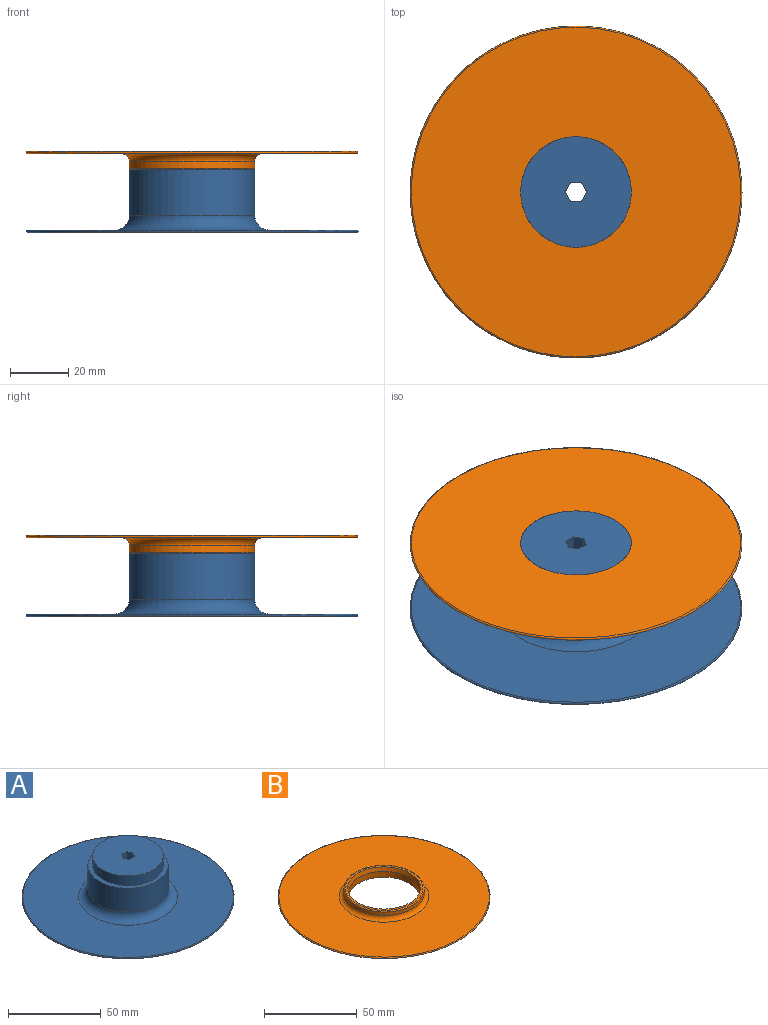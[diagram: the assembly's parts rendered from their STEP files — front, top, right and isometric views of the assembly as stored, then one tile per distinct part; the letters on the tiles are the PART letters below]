
ASSEMBLY  parts=2 mates=1
PART A: 14 faces, bbox 123.7x123.7x27.9 mm
  f0: plane 113.45x113.45mm, normal (0,0,1), area 7874.8mm2, adj f2,f13
  f1: plane 113.45x113.45mm, normal (0,0,-1), area 10074.5mm2, adj f2,f3,f4,f5,f6,f7,f9
  f2: torus R=56.73mm, axis (0,0,1), area 476.3mm2, adj f0,f1
  f3: plane 27.94x3.18mm, normal (0.87,-0.5,0), area 102.4mm2, adj f1,f4,f9,f10
  f4: plane 27.94x3.67mm, normal (0,-1,0), area 102.4mm2, adj f1,f3,f5,f10
  f5: plane 27.94x3.18mm, normal (-0.87,-0.5,0), area 102.4mm2, adj f1,f4,f6,f10
  f6: plane 27.94x3.18mm, normal (-0.87,0.5,0), area 102.4mm2, adj f1,f5,f7,f10
  f7: plane 27.94x3.67mm, normal (0,1,0), area 102.4mm2, adj f1,f6,f9,f10
  f8: cylinder r=19.05mm len=38.1mm, axis (0,0,-1), area 760.1mm2, adj f10,f12
  f9: plane 27.94x3.18mm, normal (0.87,0.5,0), area 102.4mm2, adj f1,f3,f7,f10
  f10: plane 38.1x38.1mm, normal (0,0,1), area 1105.2mm2, adj f3,f4,f5,f6,f7,f8,f9
  f11: cylinder r=21.59mm len=43.18mm, axis (0,0,-1), area 2124.8mm2, adj f12,f13
  f12: plane 43.18x43.18mm, normal (0,0,1), area 324.3mm2, adj f8,f11
  f13: torus R=26.67mm, axis (0,0,1), area 1175mm2, adj f0,f11
PART B: 9 faces, bbox 123.7x123.7x6.4 mm
  f0: plane 113.45x113.45mm, normal (0,0,1), area 8280.2mm2, adj f5,f7
  f1: plane 113.45x113.45mm, normal (0,0,-1), area 8969.3mm2, adj f2,f5
  f2: cylinder r=19.05mm len=38.1mm, axis (0,0,-1), area 456mm2, adj f1,f8
  f3: cylinder r=21.59mm len=43.18mm, axis (0,0,-1), area 315.8mm2, adj f6,f7
  f4: plane 41.91x41.91mm, normal (0,0,1), area 162.1mm2, adj f6,f8
  f5: torus R=56.73mm, axis (0,0,1), area 476.3mm2, adj f0,f1
  f6: torus R=20.96mm, axis (0,0,1), area 133.9mm2, adj f3,f4
  f7: torus R=24.13mm, axis (0,0,1), area 564.4mm2, adj f0,f3
  f8: cone r=19.05mm half-angle=14deg, axis (0,0,1), area 318.6mm2, adj f2,f4
PLACE A t=(-53.44,0,-25.42)mm
PLACE B rot(axis=(0,1,0),180deg) t=(-53.44,0,2.52)mm
MATE cylindrical A.f8 <-> B.f2  axis (0,0,1) through (-53.44,0,2.52)mm
